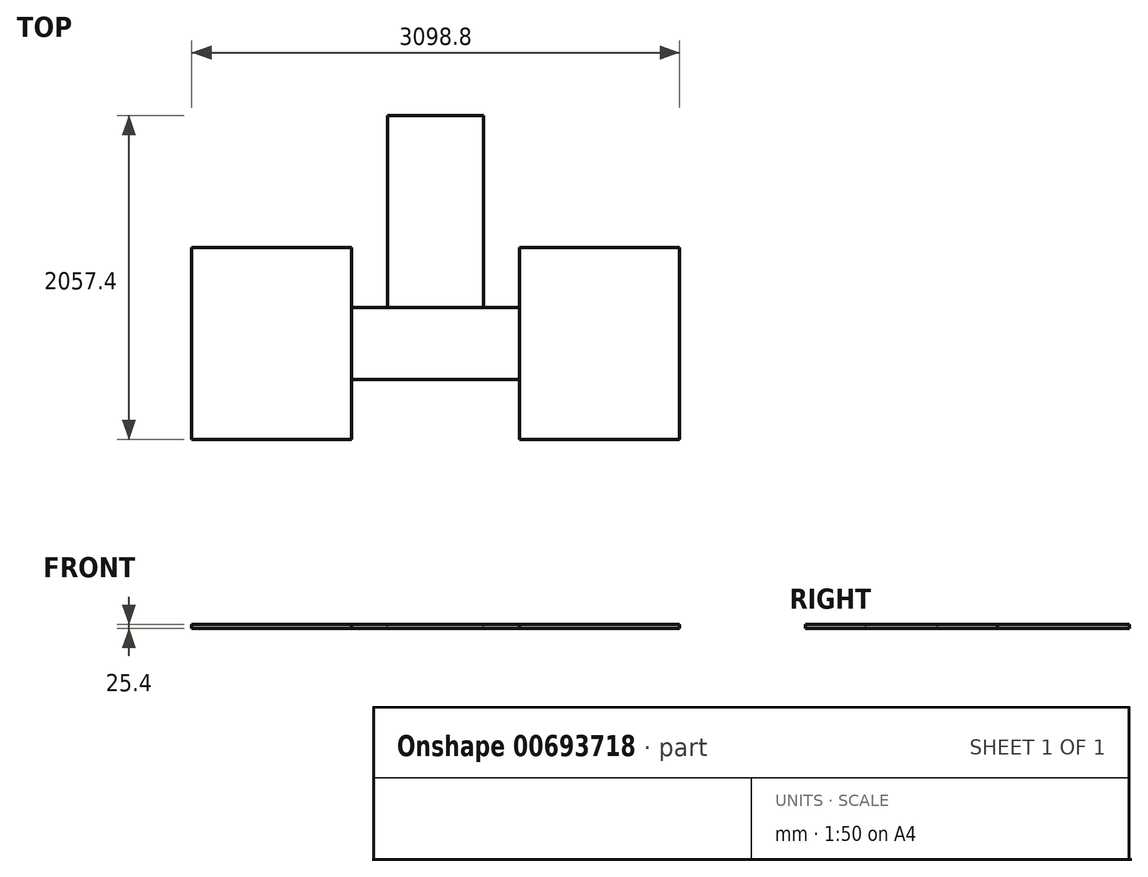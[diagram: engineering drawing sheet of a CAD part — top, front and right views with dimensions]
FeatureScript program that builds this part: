
annotation { "Feature Type Name" : "Feature", "Feature Type Description" : "" }
export const myFeature = defineFeature(function(context is Context, id is Id, definition is map)
    precondition{}
    {
        {
            var Q0;
            Q0=qCreatedBy(makeId("Top.planeOp"),FACE);
            var sketch = newSketch(context, id + "F0", { "sketchPlane" : qUnion([Q0])});
            skLineSegment(sketch, "E0.bottom", {"start": v(0, 0) * mm, "end": v(1066.8, 0) * mm});
            skLineSegment(sketch, "E0.top", {"start": v(0, 457.2) * mm, "end": v(1066.8, 457.2) * mm});
            skLineSegment(sketch, "E0.left", {"start": v(0, 0) * mm, "end": v(0, 457.2) * mm});
            skLineSegment(sketch, "E0.right", {"start": v(1066.8, 0) * mm, "end": v(1066.8, 457.2) * mm});
            skSolve(sketch);
        }
        {
            var Q0;
            Q0 = qSketchRegion(id + "F0", true);
            extrude(context, id + "F1", {"entities" : qUnion([Q0]), "depth" : 25.4 * mm, "offsetDistance" : 25.4 * mm});
        }
        {
            var Q0;
            Q0=makeQuery(id+"F1.opExtrude","CAP_FACE",FACE,{"disambiguationData":[OSD([sQuery(id+"F0.wireOp",EDGE,"E0.bottom"),sQuery(id+"F0.wireOp",EDGE,"E0.top"),sQuery(id+"F0.wireOp",EDGE,"E0.left"),sQuery(id+"F0.wireOp",EDGE,"E0.right")])],"isStart":false});
            var sketch = newSketch(context, id + "F2", { "sketchPlane" : qUnion([Q0])});
            skPoint(sketch, "E1", {"position": v(0, 228.6) * mm});
            skPoint(sketch, "E2", {"position": v(1066.8, 228.6) * mm});
            skPoint(sketch, "E3", {"position": v(0, -381) * mm});
            skLineSegment(sketch, "E4.bottom", {"start": v(0, -381) * mm, "end": v(-1016, -381) * mm});
            skLineSegment(sketch, "E4.top", {"start": v(0, 838.2) * mm, "end": v(-1016, 838.2) * mm});
            skLineSegment(sketch, "E4.left", {"start": v(0, -381) * mm, "end": v(0, 838.2) * mm});
            skLineSegment(sketch, "E4.right", {"start": v(-1016, -381) * mm, "end": v(-1016, 838.2) * mm});
            skLineSegment(sketch, "E5", {"start": v(533.4, 1561.47) * mm, "end": v(533.4, -814.7) * mm});
            skPoint(sketch, "E5.startSnap0", {"position": v(533.4, 457.2) * mm});
            skPoint(sketch, "E6.MirrorP", {"position": v(1066.8, -381) * mm});
            skLineSegment(sketch, "E7.MirrorCS", {"start": v(1066.8, -381) * mm, "end": v(2082.8, -381) * mm});
            skLineSegment(sketch, "E8.MirrorCS", {"start": v(1066.8, 838.2) * mm, "end": v(2082.8, 838.2) * mm});
            skLineSegment(sketch, "E9.MirrorCS", {"start": v(1066.8, -381) * mm, "end": v(1066.8, 838.2) * mm});
            skLineSegment(sketch, "E10.MirrorCS", {"start": v(2082.8, -381) * mm, "end": v(2082.8, 838.2) * mm});
            skSolve(sketch);
        }
        {
            var Q0;
            Q0 = qSketchRegion(id + "F2", true);
            extrude(context, id + "F3", {"entities" : qUnion([Q0]), "oppositeDirection" : true, "depth" : 25.4 * mm, "offsetDistance" : 25.4 * mm});
        }
        {
            var Q0;
            Q0=makeQuery(id+"F1.opExtrude","CAP_FACE",FACE,{"disambiguationData":[OSD([sQuery(id+"F0.wireOp",EDGE,"E0.bottom"),sQuery(id+"F0.wireOp",EDGE,"E0.top"),sQuery(id+"F0.wireOp",EDGE,"E0.left"),sQuery(id+"F0.wireOp",EDGE,"E0.right")])],"isStart":false});
            var sketch = newSketch(context, id + "F4", { "sketchPlane" : qUnion([Q0])});
            skPoint(sketch, "E11", {"position": v(533.4, 457.2) * mm});
            skPoint(sketch, "E12", {"position": v(228.6, 457.2) * mm});
            skLineSegment(sketch, "E13.bottom", {"start": v(228.6, 457.2) * mm, "end": v(838.2, 457.2) * mm});
            skLineSegment(sketch, "E13.top", {"start": v(228.6, 1676.4) * mm, "end": v(838.2, 1676.4) * mm});
            skLineSegment(sketch, "E13.left", {"start": v(228.6, 457.2) * mm, "end": v(228.6, 1676.4) * mm});
            skLineSegment(sketch, "E13.right", {"start": v(838.2, 457.2) * mm, "end": v(838.2, 1676.4) * mm});
            skSolve(sketch);
        }
        {
            var Q0;
            Q0 = qSketchRegion(id + "F4", true);
            extrude(context, id + "F5", {"entities" : qUnion([Q0]), "oppositeDirection" : true, "depth" : 25.4 * mm, "offsetDistance" : 25.4 * mm});
        }
    });
